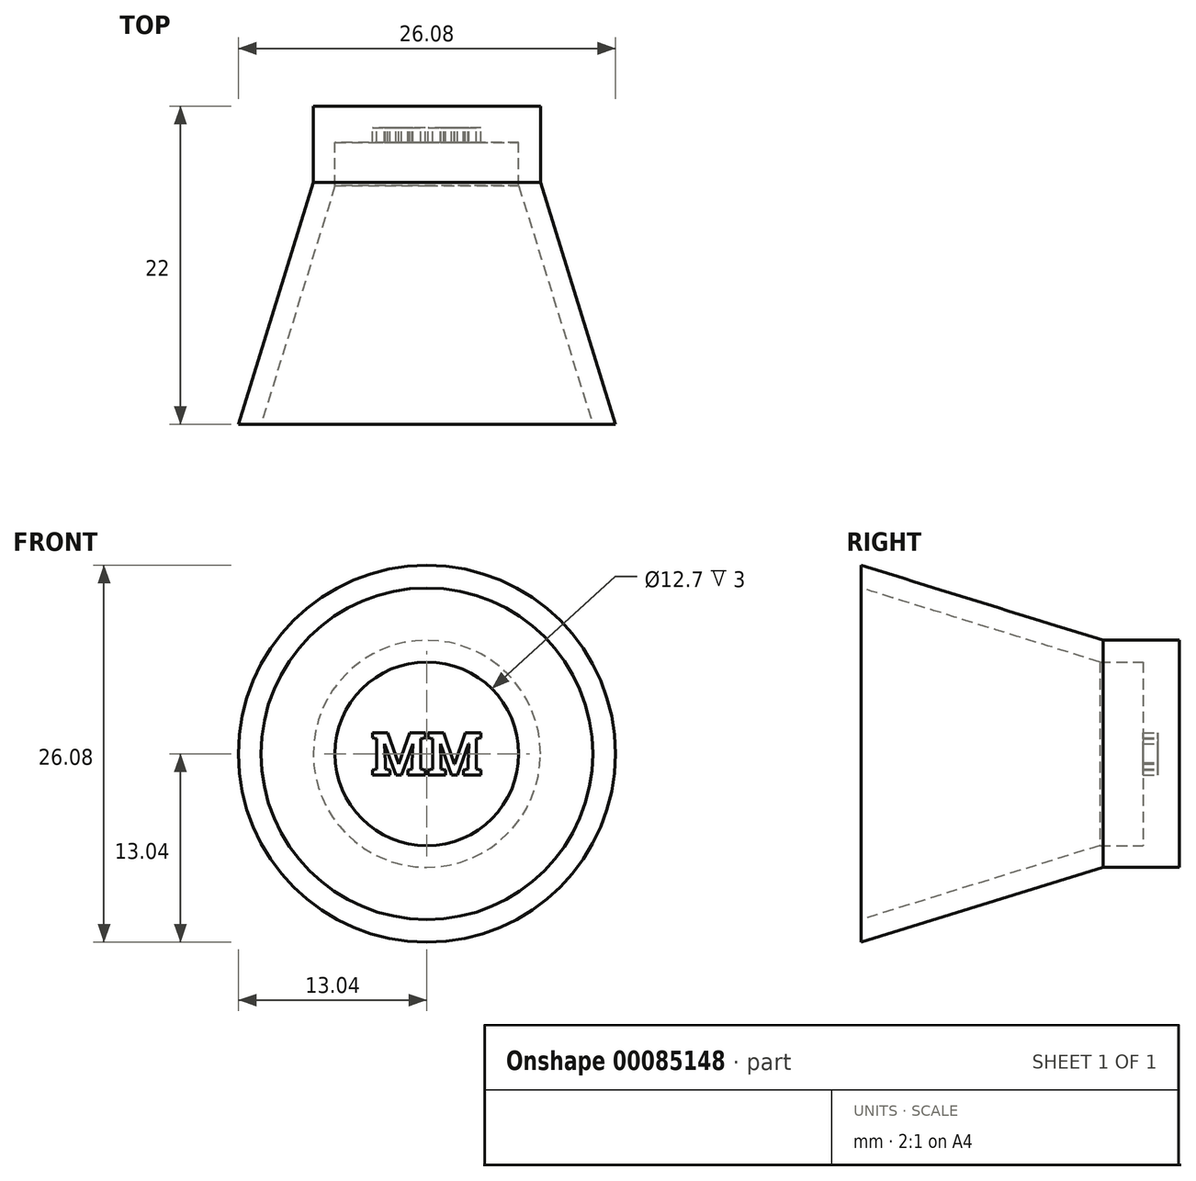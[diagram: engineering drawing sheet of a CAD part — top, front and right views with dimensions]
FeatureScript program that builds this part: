
annotation { "Feature Type Name" : "Feature", "Feature Type Description" : "" }
export const myFeature = defineFeature(function(context is Context, id is Id, definition is map)
    precondition{}
    {
        {
            var Q0;
            Q0=qCreatedBy(makeId("Top.planeOp"),FACE);
            var sketch = newSketch(context, id + "F0", { "sketchPlane" : qUnion([Q0])});
            skLineSegment(sketch, "E0", {"start": v(7.85, -1.28) * mm, "end": v(13.04, -18) * mm});
            skLineSegment(sketch, "E1", {"start": v(13.04, -18) * mm, "end": v(11.47, -18) * mm});
            skLineSegment(sketch, "E2", {"start": v(11.47, -18) * mm, "end": v(6.35, -1.5) * mm});
            skPoint(sketch, "E3.start.orphan", {"position": v(0, 0) * mm});
            skLineSegment(sketch, "E4", {"start": v(0, 4) * mm, "end": v(7.85, 4) * mm});
            skLineSegment(sketch, "E5", {"start": v(7.85, 4) * mm, "end": v(7.85, -1.28) * mm});
            skLineSegment(sketch, "E6", {"start": v(0, 2.5) * mm, "end": v(6.35, 2.5) * mm});
            skLineSegment(sketch, "E7", {"start": v(6.35, 2.5) * mm, "end": v(6.35, -1.5) * mm});
            skPoint(sketch, "E8.start.orphan", {"position": v(0, -1.5) * mm});
            skPoint(sketch, "E9.end.orphan", {"position": v(0, -18) * mm});
            skLineSegment(sketch, "E10", {"start": v(0, 4) * mm, "end": v(0, -18) * mm, "construction": true});
            skLineSegment(sketch, "E11", {"start": v(0, 4) * mm, "end": v(0, 2.5) * mm});
            skLineSegment(sketch, "E12", {"start": v(11.47, -18) * mm, "end": v(0, -18) * mm, "construction": true});
            skSolve(sketch);
        }
        {
            var Q0;
            Q0 = qSketchRegion(id + "F0", true);
            var Q1;
            Q1=sQuery(id+"F0.wireOp",EDGE,"E10");
            revolve(context, id + "F1", {"entities" : qUnion([Q0]), "axis" : qUnion([Q1]), "revolveType" : RevolveType.FULL});
        }
        {
            var Q0;
            Q0=makeQuery(id+"F1.opRevolve","SWEPT_FACE",FACE,{"disambiguationData":[OSD([sQuery(id+"F0.wireOp",EDGE,"E6")])]});
            var sketch = newSketch(context, id + "F2", { "sketchPlane" : qUnion([Q0])});
            skText(sketch, "E13", { "text": "MM", "fontName": "RobotoSlab-Bold.ttf"});
            const initialGuessF2  = {"E13": [-0.00388, -0.00147, 1, 0, 0.00295]};
            skSetInitialGuess(sketch, initialGuessF2);
            skSolve(sketch);
        }
        {
            var Q0;
            Q0=makeQuery(id+"F2.imprint","IMPRINT",FACE,{"disambiguationData":[TD([[makeQuery(id+"F2.imprint","IMPRINT",EDGE,{"derivedFrom":sQuery(id+"F2.wireOp",EDGE,"E13.sketch_text.stroke-0")}),1.0]])]});
            extrude(context, id + "F3", {"entities" : qUnion([Q0]), "operationType" : NewBodyOperationType.ADD, "depth" : 1 * mm});
        }
    });
